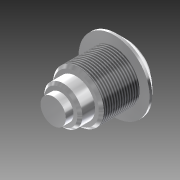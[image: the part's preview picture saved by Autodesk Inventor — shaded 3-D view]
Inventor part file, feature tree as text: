
AUTODESK INVENTOR PART (.ipt)
format: ipt  version: 2015 (Build 190159000, 159)  size: 135,680 bytes
history: native  units: mm
features: extrude x2, revolve x1, thread x1, chamfer x1
ambient origin geometry x8: Origin, YZ Plane, XZ Plane, XY Plane, X Axis, Y Axis, Z Axis, Center Point
bodies: Solid1 (feature_tree)
feature tree (5):
  revolve  "Revolución1"  [1 undecoded]
  thread  "Rosca1"  [1 undecoded]
  chamfer  "Chaflán1"  Distance=4.0mm
  extrude  "Extrusión1"  Depth=1.0mm
  extrude  "Extrusión2"  Depth=28.0mm
note: 2 required parameter values undecoded (feature->parameter linkage not recoverable at this tier; creation-order binding heuristic only, values carry confidence <= 0.55)